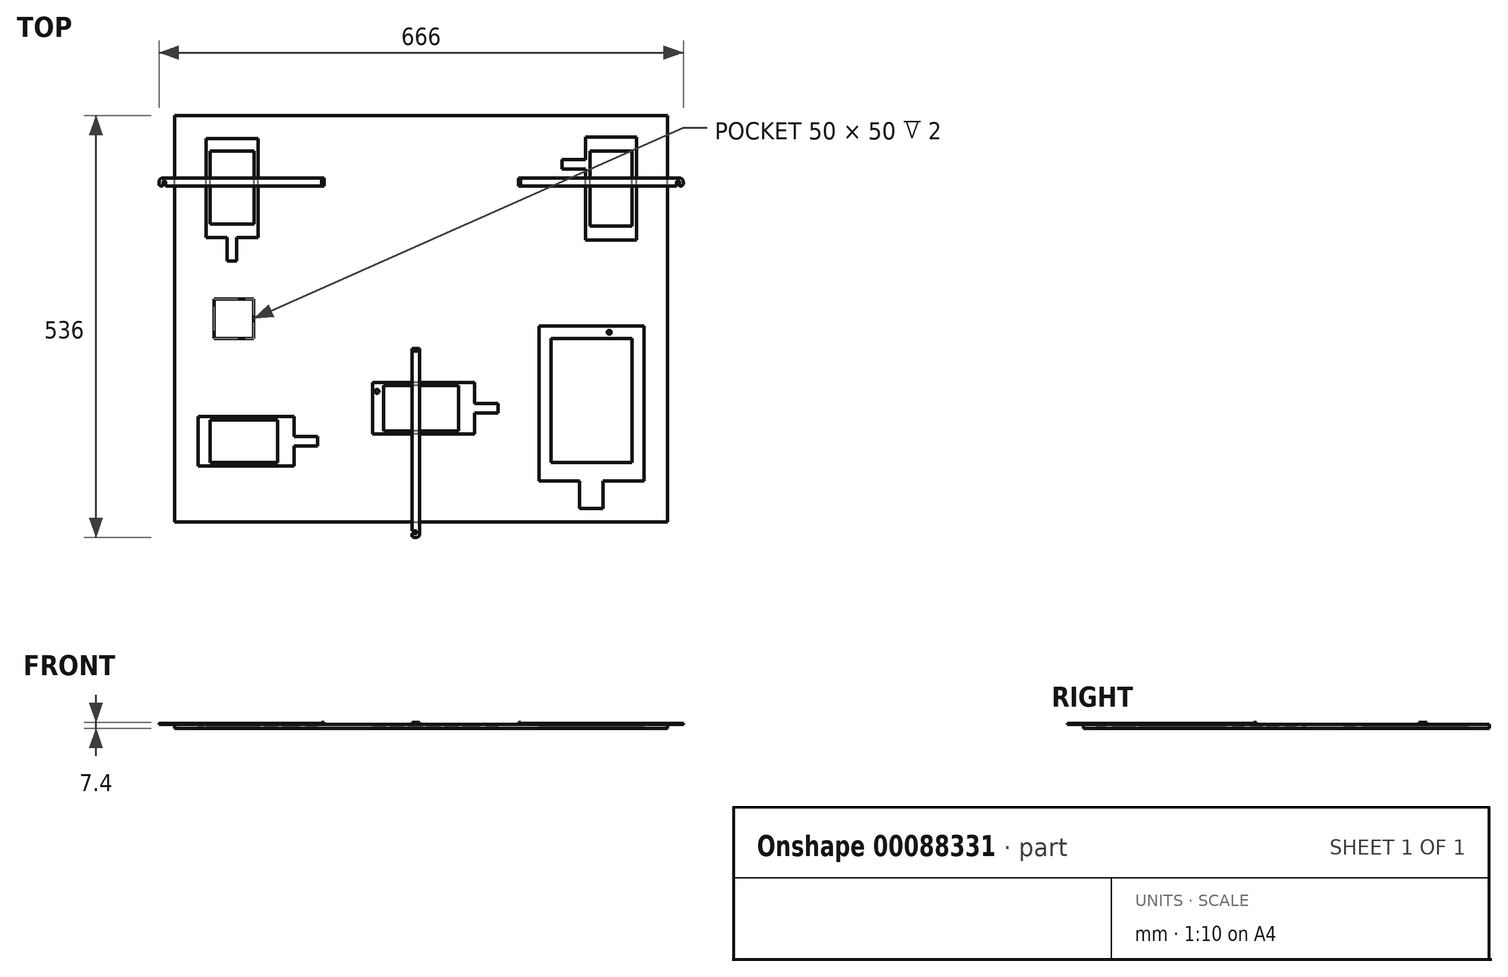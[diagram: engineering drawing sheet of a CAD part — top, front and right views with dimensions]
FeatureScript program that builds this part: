
annotation { "Feature Type Name" : "Feature", "Feature Type Description" : "" }
export const myFeature = defineFeature(function(context is Context, id is Id, definition is map)
    precondition{}
    {
        {
            var Q0;
            Q0=qCreatedBy(makeId("Top.planeOp"),FACE);
            var sketch = newSketch(context, id + "F0", { "sketchPlane" : qUnion([Q0])});
            skLineSegment(sketch, "E0.bottom", {"start": v(0, 0) * mm, "end": v(626, 0) * mm});
            skLineSegment(sketch, "E0.top", {"start": v(0, 516) * mm, "end": v(626, 516) * mm});
            skLineSegment(sketch, "E0.left", {"start": v(0, 0) * mm, "end": v(0, 516) * mm});
            skLineSegment(sketch, "E0.right", {"start": v(626, 0) * mm, "end": v(626, 516) * mm});
            skPoint(sketch, "E1", {"position": v(313, 258) * mm});
            skSolve(sketch);
        }
        {
            var Q0;
            Q0=makeQuery(id+"F0.imprint","IMPRINT",FACE,{"disambiguationData":[TD([[makeQuery(id+"F0.imprint","IMPRINT",EDGE,{"derivedFrom":sQuery(id+"F0.wireOp",EDGE,"E0.bottom")}),1.0]])]});
            extrude(context, id + "F1", {"entities" : qUnion([Q0]), "depth" : 5 * mm});
        }
        {
            var Q0;
            Q0=makeQuery(id+"F1.opExtrude","CAP_FACE",FACE,{"disambiguationData":[OSD([sQuery(id+"F0.wireOp",EDGE,"E0.bottom"),sQuery(id+"F0.wireOp",EDGE,"E0.top"),sQuery(id+"F0.wireOp",EDGE,"E0.left"),sQuery(id+"F0.wireOp",EDGE,"E0.right")])],"isStart":false});
            var sketch = newSketch(context, id + "F2", { "sketchPlane" : qUnion([Q0])});
            skLineSegment(sketch, "E2.bottom", {"start": v(586.8, 358.1) * mm, "end": v(521.8, 358.1) * mm});
            skLineSegment(sketch, "E2.top", {"start": v(586.8, 489) * mm, "end": v(521.8, 489) * mm});
            skLineSegment(sketch, "E2.left", {"start": v(586.8, 358.1) * mm, "end": v(586.8, 489) * mm});
            skLineSegment(sketch, "E2.right", {"start": v(521.8, 358.1) * mm, "end": v(521.8, 489) * mm});
            skPoint(sketch, "E2.middle", {"position": v(554.3, 423.55) * mm});
            skLineSegment(sketch, "E3.bottom", {"start": v(581, 375.9) * mm, "end": v(527.6, 375.9) * mm});
            skLineSegment(sketch, "E3.top", {"start": v(581, 471) * mm, "end": v(527.6, 471) * mm});
            skLineSegment(sketch, "E3.left", {"start": v(581, 375.9) * mm, "end": v(581, 471) * mm});
            skLineSegment(sketch, "E3.right", {"start": v(527.6, 375.9) * mm, "end": v(527.6, 471) * mm});
            skPoint(sketch, "E3.middle", {"position": v(554.3, 423.45) * mm});
            skLineSegment(sketch, "E4.bottom", {"start": v(521.8, 448) * mm, "end": v(491.8, 448) * mm});
            skLineSegment(sketch, "E4.top", {"start": v(521.8, 460) * mm, "end": v(491.8, 460) * mm});
            skLineSegment(sketch, "E4.left", {"start": v(521.8, 448) * mm, "end": v(521.8, 460) * mm});
            skLineSegment(sketch, "E4.right", {"start": v(491.8, 448) * mm, "end": v(491.8, 460) * mm});
            skPoint(sketch, "E4.middle", {"position": v(506.8, 454) * mm});
            skSolve(sketch);
        }
        {
            var Q0;
            Q0=makeQuery(id+"F1.opExtrude","CAP_FACE",FACE,{"disambiguationData":[OSD([sQuery(id+"F0.wireOp",EDGE,"E0.bottom"),sQuery(id+"F0.wireOp",EDGE,"E0.top"),sQuery(id+"F0.wireOp",EDGE,"E0.left"),sQuery(id+"F0.wireOp",EDGE,"E0.right")])],"isStart":false});
            var sketch = newSketch(context, id + "F3", { "sketchPlane" : qUnion([Q0])});
            skLineSegment(sketch, "E5.bottom", {"start": v(380.65, 111.45) * mm, "end": v(251.35, 111.45) * mm});
            skLineSegment(sketch, "E5.top", {"start": v(380.65, 176.75) * mm, "end": v(251.35, 176.75) * mm});
            skLineSegment(sketch, "E5.left", {"start": v(380.65, 111.45) * mm, "end": v(380.65, 176.75) * mm});
            skLineSegment(sketch, "E5.right", {"start": v(251.35, 111.45) * mm, "end": v(251.35, 176.75) * mm});
            skPoint(sketch, "E5.middle", {"position": v(316, 144.1) * mm});
            skLineSegment(sketch, "E6.bottom", {"start": v(360.65, 115) * mm, "end": v(265.35, 115) * mm});
            skLineSegment(sketch, "E6.top", {"start": v(360.65, 173.2) * mm, "end": v(265.35, 173.2) * mm});
            skLineSegment(sketch, "E6.left", {"start": v(360.65, 115) * mm, "end": v(360.65, 173.2) * mm});
            skLineSegment(sketch, "E6.right", {"start": v(265.35, 115) * mm, "end": v(265.35, 173.2) * mm});
            skPoint(sketch, "E6.middle", {"position": v(313, 144.1) * mm});
            skCircle(sketch, "E7", {"center": v(256.85, 165.65) * mm, "radius": 2.5 * mm});
            skLineSegment(sketch, "E8.bottom", {"start": v(410.65, 150.1) * mm, "end": v(380.65, 150.1) * mm});
            skLineSegment(sketch, "E8.top", {"start": v(410.65, 138.1) * mm, "end": v(380.65, 138.1) * mm});
            skLineSegment(sketch, "E8.left", {"start": v(410.65, 150.1) * mm, "end": v(410.65, 138.1) * mm});
            skLineSegment(sketch, "E8.right", {"start": v(380.65, 150.1) * mm, "end": v(380.65, 138.1) * mm});
            skPoint(sketch, "E8.middle", {"position": v(395.65, 144.1) * mm});
            skSolve(sketch);
        }
        {
            var Q0;
            Q0=makeQuery(id+"F2.imprint","IMPRINT",FACE,{"disambiguationData":[TD([[makeQuery(id+"F2.imprint","IMPRINT",EDGE,{"derivedFrom":sQuery(id+"F2.wireOp",EDGE,"E2.bottom")}),1.0]])]});
            var sketch = newSketch(context, id + "F4", { "sketchPlane" : qUnion([Q0])});
            skLineSegment(sketch, "E9.bottom", {"start": v(105.85, 361.3) * mm, "end": v(39.75, 361.3) * mm});
            skLineSegment(sketch, "E9.top", {"start": v(105.85, 486.6) * mm, "end": v(39.75, 486.6) * mm});
            skLineSegment(sketch, "E9.left", {"start": v(105.85, 361.3) * mm, "end": v(105.85, 486.6) * mm});
            skLineSegment(sketch, "E9.right", {"start": v(39.75, 361.3) * mm, "end": v(39.75, 486.6) * mm});
            skPoint(sketch, "E9.middle", {"position": v(72.8, 423.95) * mm});
            skLineSegment(sketch, "E10.bottom", {"start": v(100.6, 378) * mm, "end": v(45, 378) * mm});
            skLineSegment(sketch, "E10.top", {"start": v(100.6, 471) * mm, "end": v(45, 471) * mm});
            skLineSegment(sketch, "E10.left", {"start": v(100.6, 378) * mm, "end": v(100.6, 471) * mm});
            skLineSegment(sketch, "E10.right", {"start": v(45, 378) * mm, "end": v(45, 471) * mm});
            skPoint(sketch, "E10.middle", {"position": v(72.8, 424.5) * mm});
            skLineSegment(sketch, "E11.bottom", {"start": v(78.8, 331.3) * mm, "end": v(66.8, 331.3) * mm});
            skLineSegment(sketch, "E11.top", {"start": v(78.8, 361.3) * mm, "end": v(66.8, 361.3) * mm});
            skLineSegment(sketch, "E11.left", {"start": v(78.8, 331.3) * mm, "end": v(78.8, 361.3) * mm});
            skLineSegment(sketch, "E11.right", {"start": v(66.8, 331.3) * mm, "end": v(66.8, 361.3) * mm});
            skPoint(sketch, "E11.middle", {"position": v(72.8, 346.3) * mm});
            skSolve(sketch);
        }
        {
            var Q0;
            Q0=makeQuery(id+"F3.imprint","IMPRINT",FACE,{"disambiguationData":[TD([[makeQuery(id+"F3.imprint","IMPRINT",EDGE,{"derivedFrom":sQuery(id+"F3.wireOp",EDGE,"E5.bottom")}),1.0]])]});
            var sketch = newSketch(context, id + "F5", { "sketchPlane" : qUnion([Q0])});
            skLineSegment(sketch, "E12.bottom", {"start": v(595.9, 51.7) * mm, "end": v(462.9, 51.7) * mm});
            skLineSegment(sketch, "E12.top", {"start": v(595.9, 248.4) * mm, "end": v(462.9, 248.4) * mm});
            skLineSegment(sketch, "E12.left", {"start": v(595.9, 51.7) * mm, "end": v(595.9, 248.4) * mm});
            skLineSegment(sketch, "E12.right", {"start": v(462.9, 51.7) * mm, "end": v(462.9, 248.4) * mm});
            skPoint(sketch, "E12.middle", {"position": v(529.4, 150.05) * mm});
            skLineSegment(sketch, "E13.bottom", {"start": v(581, 75) * mm, "end": v(477.8, 75) * mm});
            skLineSegment(sketch, "E13.top", {"start": v(581, 233) * mm, "end": v(477.8, 233) * mm});
            skLineSegment(sketch, "E13.left", {"start": v(581, 75) * mm, "end": v(581, 233) * mm});
            skLineSegment(sketch, "E13.right", {"start": v(477.8, 75) * mm, "end": v(477.8, 233) * mm});
            skPoint(sketch, "E13.middle", {"position": v(529.4, 154) * mm});
            skCircle(sketch, "E14", {"center": v(551.9, 240.7) * mm, "radius": 2.5 * mm});
            skLineSegment(sketch, "E15.bottom", {"start": v(544.4, 51.7) * mm, "end": v(514.4, 51.7) * mm});
            skLineSegment(sketch, "E15.top", {"start": v(544.4, 16.7) * mm, "end": v(514.4, 16.7) * mm});
            skLineSegment(sketch, "E15.left", {"start": v(544.4, 51.7) * mm, "end": v(544.4, 16.7) * mm});
            skLineSegment(sketch, "E15.right", {"start": v(514.4, 51.7) * mm, "end": v(514.4, 16.7) * mm});
            skPoint(sketch, "E15.middle", {"position": v(529.4, 34.2) * mm});
            skSolve(sketch);
        }
        {
            var Q0;
            Q0=makeQuery(id+"F2.imprint","IMPRINT",FACE,{"disambiguationData":[TD([[makeQuery(id+"F2.imprint","IMPRINT",EDGE,{"derivedFrom":sQuery(id+"F2.wireOp",EDGE,"E2.bottom")}),1.0]])]});
            var sketch = newSketch(context, id + "F6", { "sketchPlane" : qUnion([Q0])});
            skLineSegment(sketch, "E16.bottom", {"start": v(151.5, 133.8) * mm, "end": v(30, 133.8) * mm});
            skLineSegment(sketch, "E16.top", {"start": v(151.5, 70.8) * mm, "end": v(30, 70.8) * mm});
            skLineSegment(sketch, "E16.left", {"start": v(151.5, 133.8) * mm, "end": v(151.5, 70.8) * mm});
            skLineSegment(sketch, "E16.right", {"start": v(30, 133.8) * mm, "end": v(30, 70.8) * mm});
            skPoint(sketch, "E16.middle", {"position": v(90.75, 102.3) * mm});
            skLineSegment(sketch, "E17.bottom", {"start": v(130.68, 129.6) * mm, "end": v(45, 129.6) * mm});
            skLineSegment(sketch, "E17.top", {"start": v(130.68, 75) * mm, "end": v(45, 75) * mm});
            skLineSegment(sketch, "E17.left", {"start": v(130.68, 129.6) * mm, "end": v(130.68, 75) * mm});
            skLineSegment(sketch, "E17.right", {"start": v(45, 129.6) * mm, "end": v(45, 75) * mm});
            skPoint(sketch, "E17.middle", {"position": v(87.84, 102.3) * mm});
            skLineSegment(sketch, "E18.bottom", {"start": v(181.5, 108.3) * mm, "end": v(151.5, 108.3) * mm});
            skLineSegment(sketch, "E18.top", {"start": v(181.5, 96.3) * mm, "end": v(151.5, 96.3) * mm});
            skLineSegment(sketch, "E18.left", {"start": v(181.5, 108.3) * mm, "end": v(181.5, 96.3) * mm});
            skLineSegment(sketch, "E18.right", {"start": v(151.5, 108.3) * mm, "end": v(151.5, 96.3) * mm});
            skPoint(sketch, "E18.middle", {"position": v(166.5, 102.3) * mm});
            skSolve(sketch);
        }
        {
            var Q0;
            {var subQ4=sQuery(id+"F2.wireOp",EDGE,"E2.bottom");Q0=makeQuery(id+"F2.imprint","IMPRINT",FACE,{"disambiguationData":[TD([[makeQuery(id+"F2.imprint","IMPRINT",EDGE,{"derivedFrom":subQ4}),1.0]])]});}
            var sketch = newSketch(context, id + "F7", { "sketchPlane" : qUnion([Q0])});
            skLineSegment(sketch, "E19.bottom", {"start": v(100, 233) * mm, "end": v(50, 233) * mm});
            skLineSegment(sketch, "E19.top", {"start": v(100, 283) * mm, "end": v(50, 283) * mm});
            skLineSegment(sketch, "E19.left", {"start": v(100, 233) * mm, "end": v(100, 283) * mm});
            skLineSegment(sketch, "E19.right", {"start": v(50, 233) * mm, "end": v(50, 283) * mm});
            skPoint(sketch, "E19.middle", {"position": v(75, 258) * mm});
            skSolve(sketch);
        }
        {
            var Q0;
            Q0 = qSketchRegion(id + "F3", true);
            var Q1;
            Q1 = qSketchRegion(id + "F4", true);
            var Q2;
            Q2 = qSketchRegion(id + "F5", true);
            var Q3;
            Q3 = qSketchRegion(id + "F2", true);
            var Q4;
            Q4 = qSketchRegion(id + "F6", true);
            var Q5;
            Q5 = qSketchRegion(id + "F7", true);
            var Q6;
            Q6=makeQuery(id+"F1.opExtrude","CAP_FACE",FACE,{"disambiguationData":[OSD([sQuery(id+"F0.wireOp",EDGE,"E0.bottom"),sQuery(id+"F0.wireOp",EDGE,"E0.top"),sQuery(id+"F0.wireOp",EDGE,"E0.left"),sQuery(id+"F0.wireOp",EDGE,"E0.right")])],"isStart":true});
            extrude(context, id + "F8", {"entities" : qUnion([Q0, Q1, Q2, Q3, Q4, Q5]), "operationType" : NewBodyOperationType.REMOVE, "oppositeDirection" : true, "endBoundEntityFace" : qUnion([Q6]), "depth" : 2 * mm});
        }
        {
            var Q0;
            {var subQ23=sQuery(id+"F0.wireOp",EDGE,"E0.bottom");var subQ24=sQuery(id+"F0.wireOp",EDGE,"E0.top");var subQ25=sQuery(id+"F0.wireOp",EDGE,"E0.left");var subQ33=sQuery(id+"F0.wireOp",EDGE,"E0.right");Q0=makeQuery(id+"F8.boolean.opBoolean","SPLIT",FACE,{"disambiguationData":[TD([makeQuery(id+"F1.opExtrude","SWEPT_FACE",FACE,{"disambiguationData":[OSD([subQ23])]})])],"derivedFrom":makeQuery(id+"F1.opExtrude","CAP_FACE",FACE,{"disambiguationData":[OSD([subQ23,subQ24,subQ25,subQ33])],"isStart":false})});}
            var sketch = newSketch(context, id + "F9", { "sketchPlane" : qUnion([Q0])});
            skLineSegment(sketch, "E20.bottom", {"start": v(-15, 436.6) * mm, "end": v(189.5, 436.6) * mm});
            skLineSegment(sketch, "E20.top", {"start": v(-17, 426.6) * mm, "end": v(-16, 426.6) * mm});
            skLineSegment(sketch, "E20.left", {"start": v(-20, 431.6) * mm, "end": v(-20, 429.6) * mm});
            skLineSegment(sketch, "E21", {"start": v(-15, 427.6) * mm, "end": v(-15, 431.6) * mm});
            skLineSegment(sketch, "E22", {"start": v(-14, 432.6) * mm, "end": v(-12.5, 432.6) * mm});
            skLineSegment(sketch, "E23", {"start": v(-11.5, 431.6) * mm, "end": v(-11.5, 427.6) * mm});
            skLineSegment(sketch, "E24.trimOffspring", {"start": v(-10.5, 426.6) * mm, "end": v(189.5, 426.6) * mm});
            skPoint(sketch, "E25.visualSharp", {"position": v(-11.5, 426.6) * mm});
            skArc(sketch, "E25.filletArc", {"start": v(-11.5, 427.6) * mm, "mid": v(-11.2, 426.9) * mm, "end": v(-10.5, 426.6) * mm});
            skPoint(sketch, "E26.visualSharp", {"position": v(-15, 426.6) * mm});
            skArc(sketch, "E26.filletArc", {"start": v(-16, 426.6) * mm, "mid": v(-15.3, 426.9) * mm, "end": v(-15, 427.6) * mm});
            skPoint(sketch, "E27.visualSharp", {"position": v(-20, 426.6) * mm});
            skArc(sketch, "E27.filletArc", {"start": v(-20, 429.6) * mm, "mid": v(-19.12, 427.48) * mm, "end": v(-17, 426.6) * mm});
            skPoint(sketch, "E28.visualSharp", {"position": v(-20, 436.6) * mm});
            skArc(sketch, "E28.filletArc", {"start": v(-15, 436.6) * mm, "mid": v(-18.54, 435.14) * mm, "end": v(-20, 431.6) * mm});
            skPoint(sketch, "E29.visualSharp", {"position": v(189.5, 436.6) * mm});
            skPoint(sketch, "E30.visualSharp", {"position": v(189.5, 426.6) * mm});
            skPoint(sketch, "E31.visualSharp", {"position": v(-11.5, 432.6) * mm});
            skArc(sketch, "E31.filletArc", {"start": v(-11.5, 431.6) * mm, "mid": v(-11.8, 432.3) * mm, "end": v(-12.5, 432.6) * mm});
            skPoint(sketch, "E32.visualSharp", {"position": v(-15, 432.6) * mm});
            skArc(sketch, "E32.filletArc", {"start": v(-14, 432.6) * mm, "mid": v(-14.7, 432.3) * mm, "end": v(-15, 431.6) * mm});
            skLineSegment(sketch, "E33", {"start": v(189.5, 436.6) * mm, "end": v(189.5, 426.6) * mm});
            skLineSegment(sketch, "E34", {"start": v(313, 258) * mm, "end": v(313, 516) * mm, "construction": true});
            skLineSegment(sketch, "E35.MirrorCS", {"start": v(643, 426.6) * mm, "end": v(642, 426.6) * mm});
            skLineSegment(sketch, "E36.MirrorCS", {"start": v(641, 427.6) * mm, "end": v(641, 431.6) * mm});
            skLineSegment(sketch, "E37.MirrorCS", {"start": v(646, 431.6) * mm, "end": v(646, 429.6) * mm});
            skLineSegment(sketch, "E38.MirrorCS", {"start": v(640, 432.6) * mm, "end": v(638.5, 432.6) * mm});
            skArc(sketch, "E39.MirrorCS", {"start": v(642, 426.6) * mm, "mid": v(641.3, 426.9) * mm, "end": v(641, 427.6) * mm});
            skArc(sketch, "E40.MirrorCS", {"start": v(641, 436.6) * mm, "mid": v(644.54, 435.14) * mm, "end": v(646, 431.6) * mm});
            skArc(sketch, "E41.MirrorCS", {"start": v(646, 429.6) * mm, "mid": v(645.12, 427.48) * mm, "end": v(643, 426.6) * mm});
            skLineSegment(sketch, "E42.MirrorCS", {"start": v(637.5, 431.6) * mm, "end": v(637.5, 427.6) * mm});
            skArc(sketch, "E43.MirrorCS", {"start": v(637.5, 427.6) * mm, "mid": v(637.2, 426.9) * mm, "end": v(636.5, 426.6) * mm});
            skArc(sketch, "E44.MirrorCS", {"start": v(637.5, 431.6) * mm, "mid": v(637.8, 432.3) * mm, "end": v(638.5, 432.6) * mm});
            skArc(sketch, "E45.MirrorCS", {"start": v(640, 432.6) * mm, "mid": v(640.7, 432.3) * mm, "end": v(641, 431.6) * mm});
            skLineSegment(sketch, "E46.MirrorCS", {"start": v(436.5, 436.6) * mm, "end": v(436.5, 426.6) * mm});
            skPoint(sketch, "E47.MirrorP", {"position": v(641, 432.6) * mm});
            skPoint(sketch, "E48.MirrorP", {"position": v(637.5, 432.6) * mm});
            skPoint(sketch, "E49.MirrorP", {"position": v(641, 426.6) * mm});
            skPoint(sketch, "E50.MirrorP", {"position": v(637.5, 426.6) * mm});
            skPoint(sketch, "E51.MirrorP", {"position": v(646, 426.6) * mm});
            skPoint(sketch, "E52.MirrorP", {"position": v(646, 436.6) * mm});
            skPoint(sketch, "E53.MirrorP", {"position": v(436.5, 426.6) * mm});
            skLineSegment(sketch, "E54.MirrorCS", {"start": v(636.5, 426.6) * mm, "end": v(436.5, 426.6) * mm});
            skLineSegment(sketch, "E55.MirrorCS", {"start": v(641, 436.6) * mm, "end": v(436.5, 436.6) * mm});
            skPoint(sketch, "E56.MirrorP", {"position": v(436.5, 436.6) * mm});
            skSolve(sketch);
        }
        {
            var Q0;
            Q0 = qSketchRegion(id + "F9", true);
            extrude(context, id + "F10", {"entities" : qUnion([Q0]), "depth" : 1.2 * mm});
        }
        {
            var Q0;
            Q0=makeQuery(id+"F10.opExtrude","SWEPT_FACE",FACE,{"disambiguationData":[OSD([sQuery(id+"F9.wireOp",EDGE,"E24.trimOffspring")])]});
            var sketch = newSketch(context, id + "F11", { "sketchPlane" : qUnion([Q0])});
            skLineSegment(sketch, "E57", {"start": v(189.5, 6.2) * mm, "end": v(189.5, 7.4) * mm});
            skLineSegment(sketch, "E58", {"start": v(189.5, 7.4) * mm, "end": v(186.5, 7.4) * mm});
            skLineSegment(sketch, "E59", {"start": v(186.5, 7.4) * mm, "end": v(187.5, 6.2) * mm});
            skLineSegment(sketch, "E60", {"start": v(187.5, 6.2) * mm, "end": v(189.5, 6.2) * mm});
            skSolve(sketch);
        }
        {
            var Q0;
            Q0=makeQuery(id+"F11.imprint","IMPRINT",FACE,{"disambiguationData":[TD([[makeQuery(id+"F11.imprint","IMPRINT",EDGE,{"derivedFrom":sQuery(id+"F11.wireOp",EDGE,"E57")}),1.0]])]});
            var Q1;
            Q1=makeQuery(id+"F10.opExtrude","SWEPT_FACE",FACE,{"disambiguationData":[OSD([sQuery(id+"F9.wireOp",EDGE,"E20.bottom")])]});
            extrude(context, id + "F12", {"entities" : qUnion([Q0]), "operationType" : NewBodyOperationType.ADD, "endBound" : BoundingType.UP_TO_SURFACE, "oppositeDirection" : true, "endBoundEntityFace" : qUnion([Q1]), "depth" : 25 * mm});
        }
        {
            var Q0;
            {var subQ23=sQuery(id+"F0.wireOp",EDGE,"E0.bottom");var subQ24=sQuery(id+"F0.wireOp",EDGE,"E0.top");var subQ25=sQuery(id+"F0.wireOp",EDGE,"E0.left");var subQ33=sQuery(id+"F0.wireOp",EDGE,"E0.right");Q0=makeQuery(id+"F8.boolean.opBoolean","SPLIT",FACE,{"disambiguationData":[TD([makeQuery(id+"F1.opExtrude","SWEPT_FACE",FACE,{"disambiguationData":[OSD([subQ23])]})])],"derivedFrom":makeQuery(id+"F1.opExtrude","CAP_FACE",FACE,{"disambiguationData":[OSD([subQ23,subQ24,subQ25,subQ33])],"isStart":false})});}
            var sketch = newSketch(context, id + "F13", { "sketchPlane" : qUnion([Q0])});
            skLineSegment(sketch, "E61.bottom", {"start": v(301.35, 220) * mm, "end": v(311.35, 220) * mm});
            skLineSegment(sketch, "E61.top", {"start": v(304.35, -20) * mm, "end": v(306.35, -20) * mm});
            skLineSegment(sketch, "E61.left", {"start": v(301.35, 220) * mm, "end": v(301.35, -10.5) * mm});
            skLineSegment(sketch, "E61.right", {"start": v(311.35, 220) * mm, "end": v(311.35, -15) * mm});
            skLineSegment(sketch, "E62.bottom", {"start": v(302.35, -15) * mm, "end": v(306.35, -15) * mm});
            skLineSegment(sketch, "E62.top", {"start": v(302.35, -11.5) * mm, "end": v(306.35, -11.5) * mm});
            skLineSegment(sketch, "E62.right", {"start": v(307.35, -14) * mm, "end": v(307.35, -12.5) * mm});
            skLineSegment(sketch, "E63.trimOffspring", {"start": v(301.35, -16) * mm, "end": v(301.35, -17) * mm});
            skPoint(sketch, "E64.visualSharp", {"position": v(311.35, -20) * mm});
            skArc(sketch, "E64.filletArc", {"start": v(306.35, -20) * mm, "mid": v(309.89, -18.54) * mm, "end": v(311.35, -15) * mm});
            skPoint(sketch, "E65.visualSharp", {"position": v(301.35, -20) * mm});
            skArc(sketch, "E65.filletArc", {"start": v(301.35, -17) * mm, "mid": v(302.23, -19.12) * mm, "end": v(304.35, -20) * mm});
            skPoint(sketch, "E66.visualSharp", {"position": v(301.35, -11.5) * mm});
            skArc(sketch, "E66.filletArc", {"start": v(301.35, -10.5) * mm, "mid": v(301.64, -11.2) * mm, "end": v(302.35, -11.5) * mm});
            skPoint(sketch, "E67.visualSharp", {"position": v(301.35, -15) * mm});
            skArc(sketch, "E67.filletArc", {"start": v(302.35, -15) * mm, "mid": v(301.64, -15.3) * mm, "end": v(301.35, -16) * mm});
            skPoint(sketch, "E68.visualSharp", {"position": v(307.35, -11.5) * mm});
            skArc(sketch, "E68.filletArc", {"start": v(307.35, -12.5) * mm, "mid": v(307.06, -11.8) * mm, "end": v(306.35, -11.5) * mm});
            skPoint(sketch, "E69.visualSharp", {"position": v(307.35, -15) * mm});
            skArc(sketch, "E69.filletArc", {"start": v(306.35, -15) * mm, "mid": v(307.06, -14.7) * mm, "end": v(307.35, -14) * mm});
            skSolve(sketch);
        }
        {
            var Q0;
            Q0 = qSketchRegion(id + "F13", true);
            extrude(context, id + "F14", {"entities" : qUnion([Q0]), "depth" : 1.2 * mm});
        }
        {
            var Q0;
            Q0=makeQuery(id+"F14.opExtrude","SWEPT_FACE",FACE,{"disambiguationData":[OSD([sQuery(id+"F13.wireOp",EDGE,"E61.left")])]});
            var sketch = newSketch(context, id + "F15", { "sketchPlane" : qUnion([Q0])});
            skLineSegment(sketch, "E70", {"start": v(-220, 6.2) * mm, "end": v(-220, 7.4) * mm});
            skLineSegment(sketch, "E71", {"start": v(-220, 7.4) * mm, "end": v(-217, 7.4) * mm});
            skLineSegment(sketch, "E72", {"start": v(-217, 7.4) * mm, "end": v(-218, 6.2) * mm});
            skLineSegment(sketch, "E73", {"start": v(-218, 6.2) * mm, "end": v(-220, 6.2) * mm});
            skSolve(sketch);
        }
        {
            var Q0;
            Q0=makeQuery(id+"F15.imprint","IMPRINT",FACE,{"disambiguationData":[TD([[makeQuery(id+"F15.imprint","IMPRINT",EDGE,{"derivedFrom":sQuery(id+"F15.wireOp",EDGE,"E70")}),-1.0]])]});
            var Q1;
            Q1=makeQuery(id+"F14.opExtrude","SWEPT_FACE",FACE,{"disambiguationData":[OSD([sQuery(id+"F13.wireOp",EDGE,"E61.right")])]});
            extrude(context, id + "F16", {"entities" : qUnion([Q0]), "operationType" : NewBodyOperationType.ADD, "endBound" : BoundingType.UP_TO_SURFACE, "oppositeDirection" : true, "endBoundEntityFace" : qUnion([Q1]), "depth" : 25 * mm});
        }
        {
            var Q0;
            Q0=makeQuery(id+"F10.opExtrude","SWEPT_FACE",FACE,{"disambiguationData":[OSD([sQuery(id+"F9.wireOp",EDGE,"E54.MirrorCS")])]});
            var sketch = newSketch(context, id + "F17", { "sketchPlane" : qUnion([Q0])});
            skLineSegment(sketch, "E74", {"start": v(436.5, 6.2) * mm, "end": v(436.5, 7.4) * mm});
            skLineSegment(sketch, "E75", {"start": v(436.5, 7.4) * mm, "end": v(439.5, 7.4) * mm});
            skLineSegment(sketch, "E76", {"start": v(439.5, 7.4) * mm, "end": v(438.5, 6.2) * mm});
            skLineSegment(sketch, "E77", {"start": v(438.5, 6.2) * mm, "end": v(436.5, 6.2) * mm});
            skSolve(sketch);
        }
        {
            var Q0;
            Q0=makeQuery(id+"F17.imprint","IMPRINT",FACE,{"disambiguationData":[TD([[makeQuery(id+"F17.imprint","IMPRINT",EDGE,{"derivedFrom":sQuery(id+"F17.wireOp",EDGE,"E74")}),-1.0]])]});
            var Q1;
            Q1=makeQuery(id+"F10.opExtrude","SWEPT_FACE",FACE,{"disambiguationData":[OSD([sQuery(id+"F9.wireOp",EDGE,"E55.MirrorCS")])]});
            extrude(context, id + "F18", {"entities" : qUnion([Q0]), "operationType" : NewBodyOperationType.ADD, "endBound" : BoundingType.UP_TO_SURFACE, "oppositeDirection" : true, "endBoundEntityFace" : qUnion([Q1]), "depth" : 25 * mm});
        }
    });
